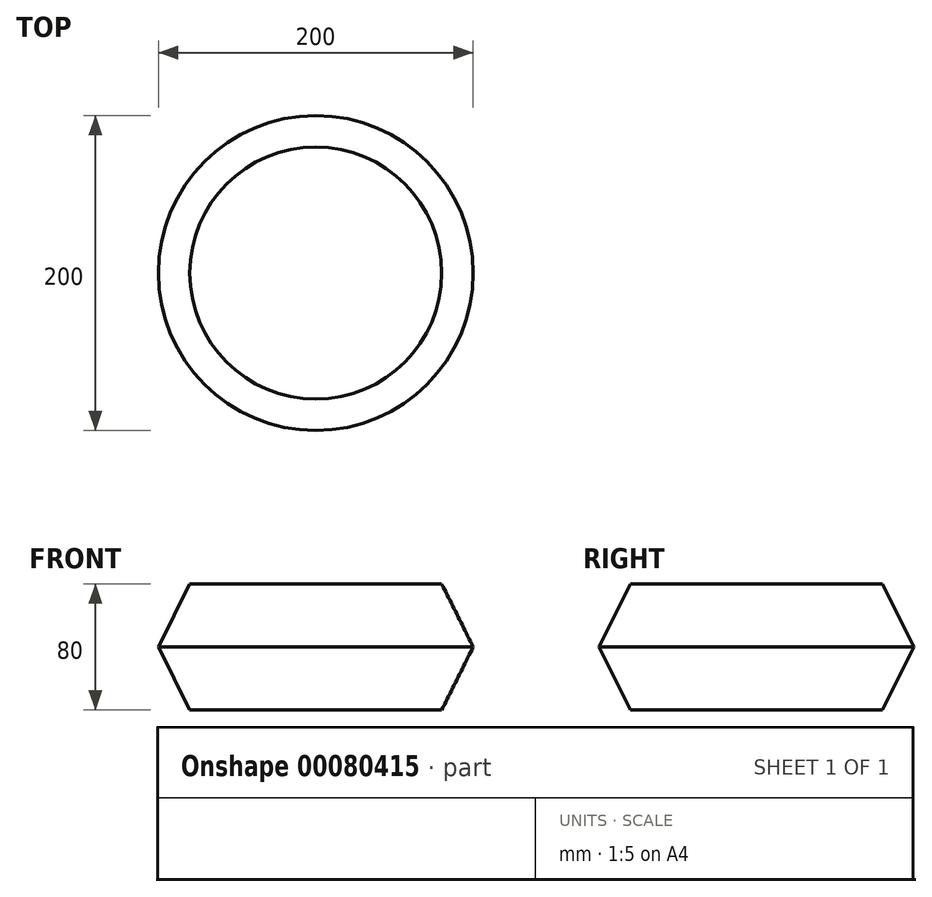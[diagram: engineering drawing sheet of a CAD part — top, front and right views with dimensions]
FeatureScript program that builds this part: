
annotation { "Feature Type Name" : "Feature", "Feature Type Description" : "" }
export const myFeature = defineFeature(function(context is Context, id is Id, definition is map)
    precondition{}
    {
        {
            var Q0;
            Q0=qCreatedBy(makeId("Top.planeOp"),FACE);
            var sketch = newSketch(context, id + "F0", { "sketchPlane" : qUnion([Q0])});
            skCircle(sketch, "E0", {"center": v(0, 0) * mm, "radius": 100 * mm});
            skSolve(sketch);
        }
        {
            var Q0;
            Q0=qCreatedBy(makeId("Top.planeOp"),FACE);
            cPlane(context, id + "F1", {"entities" : qUnion([Q0]), "cplaneType" : CPlaneType.OFFSET, "offset" : 40 * mm, "width" : 150 * mm, "height" : 150 * mm});
        }
        {
            var Q0;
            Q0=qCreatedBy(id+"F1.planeOp",FACE);
            var sketch = newSketch(context, id + "F2", { "sketchPlane" : qUnion([Q0])});
            skCircle(sketch, "E1", {"center": v(0, 0) * mm, "radius": 80 * mm});
            skSolve(sketch);
        }
        {
            var Q0;
            Q0=makeQuery(id+"F0.imprint","IMPRINT",FACE,{"disambiguationData":[TD([[makeQuery(id+"F0.imprint","IMPRINT",EDGE,{"derivedFrom":sQuery(id+"F0.wireOp",EDGE,"E0")}),1.0]])]});
            var Q1;
            Q1=makeQuery(id+"F2.imprint","IMPRINT",FACE,{"disambiguationData":[TD([[makeQuery(id+"F2.imprint","IMPRINT",EDGE,{"derivedFrom":sQuery(id+"F2.wireOp",EDGE,"E1")}),1.0]])]});
            loft(context, id + "F3", {"sheetProfilesArray" : [{ "sheetProfileEntities" : qUnion([Q0]) }, { "sheetProfileEntities" : qUnion([Q1]) }]});
        }
        {
            var Q0;
            Q0=makeQuery(id+"F3.opLoft","SWEPT_BODY",BODY,{"disambiguationData":[OSD([makeQuery(id+"F0.imprint","IMPRINT",FACE,{"disambiguationData":[TD([[makeQuery(id+"F0.imprint","IMPRINT",EDGE,{"derivedFrom":sQuery(id+"F0.wireOp",EDGE,"E0")}),1.0]])]}),makeQuery(id+"F2.imprint","IMPRINT",FACE,{"disambiguationData":[TD([[makeQuery(id+"F2.imprint","IMPRINT",EDGE,{"derivedFrom":sQuery(id+"F2.wireOp",EDGE,"E1")}),1.0]])]})])]});
            var Q1;
            Q1=qCreatedBy(makeId("Top.planeOp"),FACE);
            mirror(context, id + "F4", {"operationType" : NewBodyOperationType.ADD, "entities" : qUnion([Q0]), "mirrorPlane" : qUnion([Q1])});
        }
    });
